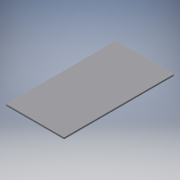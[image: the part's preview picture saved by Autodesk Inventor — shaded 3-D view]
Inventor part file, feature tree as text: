
AUTODESK INVENTOR PART (.ipt)
format: ipt  version: 2018 (Build 220112000, 112)  size: 89,600 bytes
history: native  units: in
note: dims shown in document units (in); Inventor stores cm internally (conversion verified against a paired STEP export)
features: extrude x1, sketch x1
ambient origin geometry x8: Origin, YZ Plane, XZ Plane, XY Plane, X Axis, Y Axis, Z Axis, Center Point
bodies: Solid1 (feature_tree)
feature tree (2):
  extrude  "Extrusion1"  Depth=0.75in
  sketch  "Sketch1"  dims[d0=28.226in d1=0.75in d2=53.463in d3=0.0in]
